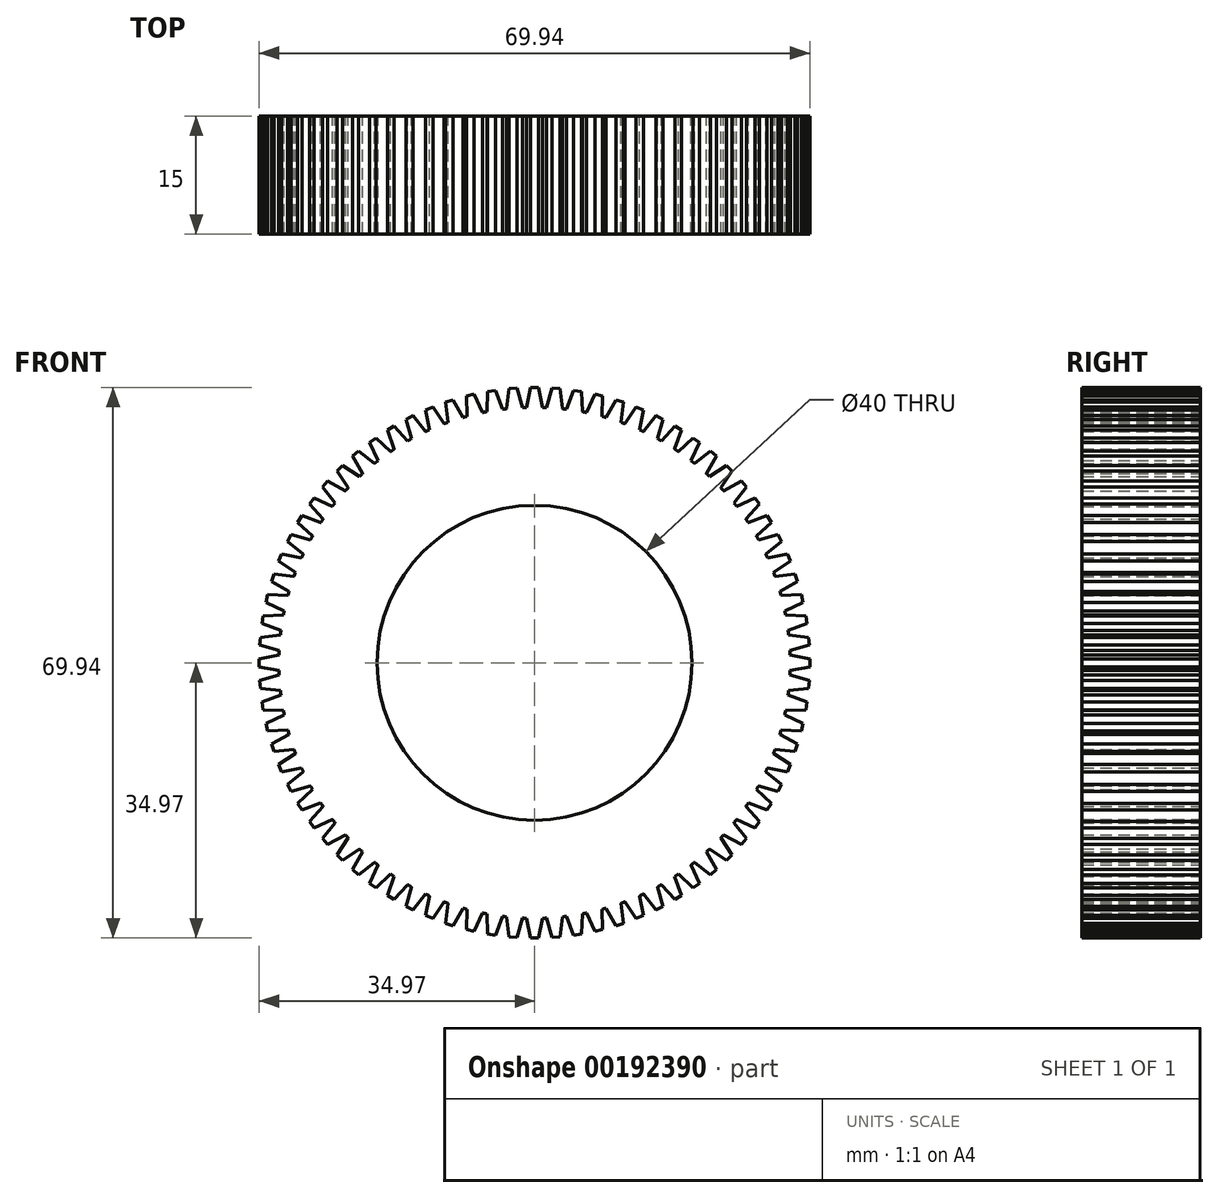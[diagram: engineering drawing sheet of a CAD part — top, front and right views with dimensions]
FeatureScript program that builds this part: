
annotation { "Feature Type Name" : "Feature", "Feature Type Description" : "" }
export const myFeature = defineFeature(function(context is Context, id is Id, definition is map)
    precondition{}
    {
        {
            var Q0;
            Q0=qCreatedBy(makeId("Front.planeOp"),FACE);
            var sketch = newSketch(context, id + "F0", { "sketchPlane" : qUnion([Q0])});
            skCircle(sketch, "E0", {"center": v(0, 0) * mm, "radius": 32.47 * mm});
            skLineSegment(sketch, "E1", {"start": v(-1, 32.45) * mm, "end": v(-0.5, 34.97) * mm});
            skLineSegment(sketch, "E2.MirrorCS", {"start": v(1, 32.45) * mm, "end": v(0.5, 34.97) * mm});
            skLineSegment(sketch, "E3", {"start": v(-0.5, 34.97) * mm, "end": v(0.5, 34.97) * mm});
            skLineSegment(sketch, "E4.1.0", {"start": v(-1.55, 32.43) * mm, "end": v(-2.25, 34.9) * mm});
            skLineSegment(sketch, "E4.1.1", {"start": v(-3.24, 34.82) * mm, "end": v(-2.25, 34.9) * mm});
            skLineSegment(sketch, "E4.1.2", {"start": v(-3.54, 32.27) * mm, "end": v(-3.24, 34.82) * mm});
            skLineSegment(sketch, "E4.2.0", {"start": v(-4.09, 32.21) * mm, "end": v(-4.98, 34.62) * mm});
            skLineSegment(sketch, "E4.2.1", {"start": v(-5.96, 34.46) * mm, "end": v(-4.98, 34.62) * mm});
            skLineSegment(sketch, "E4.2.2", {"start": v(-6.06, 31.9) * mm, "end": v(-5.96, 34.46) * mm});
            skLineSegment(sketch, "E4.3.0", {"start": v(-6.6, 31.8) * mm, "end": v(-7.68, 34.12) * mm});
            skLineSegment(sketch, "E4.3.1", {"start": v(-8.65, 33.89) * mm, "end": v(-7.68, 34.12) * mm});
            skLineSegment(sketch, "E4.3.2", {"start": v(-8.55, 31.32) * mm, "end": v(-8.65, 33.89) * mm});
            skLineSegment(sketch, "E4.4.0", {"start": v(-9.08, 31.17) * mm, "end": v(-10.33, 33.41) * mm});
            skLineSegment(sketch, "E4.4.1", {"start": v(-11.28, 33.1) * mm, "end": v(-10.33, 33.41) * mm});
            skLineSegment(sketch, "E4.4.2", {"start": v(-10.98, 30.56) * mm, "end": v(-11.28, 33.1) * mm});
            skLineSegment(sketch, "E4.5.0", {"start": v(-11.5, 30.37) * mm, "end": v(-12.92, 32.5) * mm});
            skLineSegment(sketch, "E4.5.1", {"start": v(-13.84, 32.12) * mm, "end": v(-12.92, 32.5) * mm});
            skLineSegment(sketch, "E4.5.2", {"start": v(-13.34, 29.6) * mm, "end": v(-13.84, 32.12) * mm});
            skLineSegment(sketch, "E4.6.0", {"start": v(-13.84, 29.37) * mm, "end": v(-15.43, 31.38) * mm});
            skLineSegment(sketch, "E4.6.1", {"start": v(-16.32, 30.93) * mm, "end": v(-15.43, 31.38) * mm});
            skLineSegment(sketch, "E4.6.2", {"start": v(-15.62, 28.46) * mm, "end": v(-16.32, 30.93) * mm});
            skLineSegment(sketch, "E4.7.0", {"start": v(-16.1, 28.2) * mm, "end": v(-17.84, 30.08) * mm});
            skLineSegment(sketch, "E4.7.1", {"start": v(-18.7, 29.55) * mm, "end": v(-17.84, 30.08) * mm});
            skLineSegment(sketch, "E4.7.2", {"start": v(-17.8, 27.15) * mm, "end": v(-18.7, 29.55) * mm});
            skLineSegment(sketch, "E4.8.0", {"start": v(-18.27, 26.84) * mm, "end": v(-20.15, 28.58) * mm});
            skLineSegment(sketch, "E4.8.1", {"start": v(-20.96, 28) * mm, "end": v(-20.15, 28.58) * mm});
            skLineSegment(sketch, "E4.8.2", {"start": v(-19.88, 25.67) * mm, "end": v(-20.96, 28) * mm});
            skLineSegment(sketch, "E4.9.0", {"start": v(-20.32, 25.33) * mm, "end": v(-22.33, 26.92) * mm});
            skLineSegment(sketch, "E4.9.1", {"start": v(-23.1, 26.27) * mm, "end": v(-22.33, 26.92) * mm});
            skLineSegment(sketch, "E4.9.2", {"start": v(-21.84, 24.03) * mm, "end": v(-23.1, 26.27) * mm});
            skLineSegment(sketch, "E4.10.0", {"start": v(-22.24, 23.65) * mm, "end": v(-24.37, 25.08) * mm});
            skLineSegment(sketch, "E4.10.1", {"start": v(-25.08, 24.37) * mm, "end": v(-24.37, 25.08) * mm});
            skLineSegment(sketch, "E4.10.2", {"start": v(-23.65, 22.24) * mm, "end": v(-25.08, 24.37) * mm});
            skLineSegment(sketch, "E4.11.0", {"start": v(-24.03, 21.84) * mm, "end": v(-26.27, 23.1) * mm});
            skLineSegment(sketch, "E4.11.1", {"start": v(-26.92, 22.33) * mm, "end": v(-26.27, 23.1) * mm});
            skLineSegment(sketch, "E4.11.2", {"start": v(-25.33, 20.32) * mm, "end": v(-26.92, 22.33) * mm});
            skLineSegment(sketch, "E4.12.0", {"start": v(-25.67, 19.88) * mm, "end": v(-28, 20.96) * mm});
            skLineSegment(sketch, "E4.12.1", {"start": v(-28.58, 20.15) * mm, "end": v(-28, 20.96) * mm});
            skLineSegment(sketch, "E4.12.2", {"start": v(-26.84, 18.27) * mm, "end": v(-28.58, 20.15) * mm});
            skLineSegment(sketch, "E4.13.0", {"start": v(-27.15, 17.8) * mm, "end": v(-29.55, 18.7) * mm});
            skLineSegment(sketch, "E4.13.1", {"start": v(-30.08, 17.84) * mm, "end": v(-29.55, 18.7) * mm});
            skLineSegment(sketch, "E4.13.2", {"start": v(-28.2, 16.1) * mm, "end": v(-30.08, 17.84) * mm});
            skLineSegment(sketch, "E4.14.0", {"start": v(-28.46, 15.62) * mm, "end": v(-30.93, 16.32) * mm});
            skLineSegment(sketch, "E4.14.1", {"start": v(-31.38, 15.43) * mm, "end": v(-30.93, 16.32) * mm});
            skLineSegment(sketch, "E4.14.2", {"start": v(-29.37, 13.84) * mm, "end": v(-31.38, 15.43) * mm});
            skLineSegment(sketch, "E4.15.0", {"start": v(-29.6, 13.34) * mm, "end": v(-32.12, 13.84) * mm});
            skLineSegment(sketch, "E4.15.1", {"start": v(-32.5, 12.92) * mm, "end": v(-32.12, 13.84) * mm});
            skLineSegment(sketch, "E4.15.2", {"start": v(-30.37, 11.5) * mm, "end": v(-32.5, 12.92) * mm});
            skLineSegment(sketch, "E4.16.0", {"start": v(-30.56, 10.98) * mm, "end": v(-33.1, 11.28) * mm});
            skLineSegment(sketch, "E4.16.1", {"start": v(-33.41, 10.33) * mm, "end": v(-33.1, 11.28) * mm});
            skLineSegment(sketch, "E4.16.2", {"start": v(-31.17, 9.08) * mm, "end": v(-33.41, 10.33) * mm});
            skLineSegment(sketch, "E4.17.0", {"start": v(-31.32, 8.55) * mm, "end": v(-33.89, 8.65) * mm});
            skLineSegment(sketch, "E4.17.1", {"start": v(-34.12, 7.68) * mm, "end": v(-33.89, 8.65) * mm});
            skLineSegment(sketch, "E4.17.2", {"start": v(-31.8, 6.6) * mm, "end": v(-34.12, 7.68) * mm});
            skLineSegment(sketch, "E4.18.0", {"start": v(-31.9, 6.06) * mm, "end": v(-34.46, 5.96) * mm});
            skLineSegment(sketch, "E4.18.1", {"start": v(-34.62, 4.98) * mm, "end": v(-34.46, 5.96) * mm});
            skLineSegment(sketch, "E4.18.2", {"start": v(-32.21, 4.09) * mm, "end": v(-34.62, 4.98) * mm});
            skLineSegment(sketch, "E4.19.0", {"start": v(-32.27, 3.54) * mm, "end": v(-34.82, 3.24) * mm});
            skLineSegment(sketch, "E4.19.1", {"start": v(-34.9, 2.25) * mm, "end": v(-34.82, 3.24) * mm});
            skLineSegment(sketch, "E4.19.2", {"start": v(-32.43, 1.55) * mm, "end": v(-34.9, 2.25) * mm});
            skLineSegment(sketch, "E4.20.0", {"start": v(-32.45, 1) * mm, "end": v(-34.97, 0.5) * mm});
            skLineSegment(sketch, "E4.20.1", {"start": v(-34.97, -0.5) * mm, "end": v(-34.97, 0.5) * mm});
            skLineSegment(sketch, "E4.20.2", {"start": v(-32.45, -1) * mm, "end": v(-34.97, -0.5) * mm});
            skLineSegment(sketch, "E4.21.0", {"start": v(-32.43, -1.55) * mm, "end": v(-34.9, -2.25) * mm});
            skLineSegment(sketch, "E4.21.1", {"start": v(-34.82, -3.24) * mm, "end": v(-34.9, -2.25) * mm});
            skLineSegment(sketch, "E4.21.2", {"start": v(-32.27, -3.54) * mm, "end": v(-34.82, -3.24) * mm});
            skLineSegment(sketch, "E4.22.0", {"start": v(-32.21, -4.09) * mm, "end": v(-34.62, -4.98) * mm});
            skLineSegment(sketch, "E4.22.1", {"start": v(-34.46, -5.96) * mm, "end": v(-34.62, -4.98) * mm});
            skLineSegment(sketch, "E4.22.2", {"start": v(-31.9, -6.06) * mm, "end": v(-34.46, -5.96) * mm});
            skLineSegment(sketch, "E4.23.0", {"start": v(-31.8, -6.6) * mm, "end": v(-34.12, -7.68) * mm});
            skLineSegment(sketch, "E4.23.1", {"start": v(-33.89, -8.65) * mm, "end": v(-34.12, -7.68) * mm});
            skLineSegment(sketch, "E4.23.2", {"start": v(-31.32, -8.55) * mm, "end": v(-33.89, -8.65) * mm});
            skLineSegment(sketch, "E4.24.0", {"start": v(-31.17, -9.08) * mm, "end": v(-33.41, -10.33) * mm});
            skLineSegment(sketch, "E4.24.1", {"start": v(-33.1, -11.28) * mm, "end": v(-33.41, -10.33) * mm});
            skLineSegment(sketch, "E4.24.2", {"start": v(-30.56, -10.98) * mm, "end": v(-33.1, -11.28) * mm});
            skLineSegment(sketch, "E4.25.0", {"start": v(-30.37, -11.5) * mm, "end": v(-32.5, -12.92) * mm});
            skLineSegment(sketch, "E4.25.1", {"start": v(-32.12, -13.84) * mm, "end": v(-32.5, -12.92) * mm});
            skLineSegment(sketch, "E4.25.2", {"start": v(-29.6, -13.34) * mm, "end": v(-32.12, -13.84) * mm});
            skLineSegment(sketch, "E4.26.0", {"start": v(-29.37, -13.84) * mm, "end": v(-31.38, -15.43) * mm});
            skLineSegment(sketch, "E4.26.1", {"start": v(-30.93, -16.32) * mm, "end": v(-31.38, -15.43) * mm});
            skLineSegment(sketch, "E4.26.2", {"start": v(-28.46, -15.62) * mm, "end": v(-30.93, -16.32) * mm});
            skLineSegment(sketch, "E4.27.0", {"start": v(-28.2, -16.1) * mm, "end": v(-30.08, -17.84) * mm});
            skLineSegment(sketch, "E4.27.1", {"start": v(-29.55, -18.7) * mm, "end": v(-30.08, -17.84) * mm});
            skLineSegment(sketch, "E4.27.2", {"start": v(-27.15, -17.8) * mm, "end": v(-29.55, -18.7) * mm});
            skLineSegment(sketch, "E4.28.0", {"start": v(-26.84, -18.27) * mm, "end": v(-28.58, -20.15) * mm});
            skLineSegment(sketch, "E4.28.1", {"start": v(-28, -20.96) * mm, "end": v(-28.58, -20.15) * mm});
            skLineSegment(sketch, "E4.28.2", {"start": v(-25.67, -19.88) * mm, "end": v(-28, -20.96) * mm});
            skLineSegment(sketch, "E4.29.0", {"start": v(-25.33, -20.32) * mm, "end": v(-26.92, -22.33) * mm});
            skLineSegment(sketch, "E4.29.1", {"start": v(-26.27, -23.1) * mm, "end": v(-26.92, -22.33) * mm});
            skLineSegment(sketch, "E4.29.2", {"start": v(-24.03, -21.84) * mm, "end": v(-26.27, -23.1) * mm});
            skLineSegment(sketch, "E4.30.0", {"start": v(-23.65, -22.24) * mm, "end": v(-25.08, -24.37) * mm});
            skLineSegment(sketch, "E4.30.1", {"start": v(-24.37, -25.08) * mm, "end": v(-25.08, -24.37) * mm});
            skLineSegment(sketch, "E4.30.2", {"start": v(-22.24, -23.65) * mm, "end": v(-24.37, -25.08) * mm});
            skLineSegment(sketch, "E4.31.0", {"start": v(-21.84, -24.03) * mm, "end": v(-23.1, -26.27) * mm});
            skLineSegment(sketch, "E4.31.1", {"start": v(-22.33, -26.92) * mm, "end": v(-23.1, -26.27) * mm});
            skLineSegment(sketch, "E4.31.2", {"start": v(-20.32, -25.33) * mm, "end": v(-22.33, -26.92) * mm});
            skLineSegment(sketch, "E4.32.0", {"start": v(-19.88, -25.67) * mm, "end": v(-20.96, -28) * mm});
            skLineSegment(sketch, "E4.32.1", {"start": v(-20.15, -28.58) * mm, "end": v(-20.96, -28) * mm});
            skLineSegment(sketch, "E4.32.2", {"start": v(-18.27, -26.84) * mm, "end": v(-20.15, -28.58) * mm});
            skLineSegment(sketch, "E4.33.0", {"start": v(-17.8, -27.15) * mm, "end": v(-18.7, -29.55) * mm});
            skLineSegment(sketch, "E4.33.1", {"start": v(-17.84, -30.08) * mm, "end": v(-18.7, -29.55) * mm});
            skLineSegment(sketch, "E4.33.2", {"start": v(-16.1, -28.2) * mm, "end": v(-17.84, -30.08) * mm});
            skLineSegment(sketch, "E4.34.0", {"start": v(-15.62, -28.46) * mm, "end": v(-16.32, -30.93) * mm});
            skLineSegment(sketch, "E4.34.1", {"start": v(-15.43, -31.38) * mm, "end": v(-16.32, -30.93) * mm});
            skLineSegment(sketch, "E4.34.2", {"start": v(-13.84, -29.37) * mm, "end": v(-15.43, -31.38) * mm});
            skLineSegment(sketch, "E4.35.0", {"start": v(-13.34, -29.6) * mm, "end": v(-13.84, -32.12) * mm});
            skLineSegment(sketch, "E4.35.1", {"start": v(-12.92, -32.5) * mm, "end": v(-13.84, -32.12) * mm});
            skLineSegment(sketch, "E4.35.2", {"start": v(-11.5, -30.37) * mm, "end": v(-12.92, -32.5) * mm});
            skLineSegment(sketch, "E4.36.0", {"start": v(-10.98, -30.56) * mm, "end": v(-11.28, -33.1) * mm});
            skLineSegment(sketch, "E4.36.1", {"start": v(-10.33, -33.41) * mm, "end": v(-11.28, -33.1) * mm});
            skLineSegment(sketch, "E4.36.2", {"start": v(-9.08, -31.17) * mm, "end": v(-10.33, -33.41) * mm});
            skLineSegment(sketch, "E4.37.0", {"start": v(-8.55, -31.32) * mm, "end": v(-8.65, -33.89) * mm});
            skLineSegment(sketch, "E4.37.1", {"start": v(-7.68, -34.12) * mm, "end": v(-8.65, -33.89) * mm});
            skLineSegment(sketch, "E4.37.2", {"start": v(-6.6, -31.8) * mm, "end": v(-7.68, -34.12) * mm});
            skLineSegment(sketch, "E4.38.0", {"start": v(-6.06, -31.9) * mm, "end": v(-5.96, -34.46) * mm});
            skLineSegment(sketch, "E4.38.1", {"start": v(-4.98, -34.62) * mm, "end": v(-5.96, -34.46) * mm});
            skLineSegment(sketch, "E4.38.2", {"start": v(-4.09, -32.21) * mm, "end": v(-4.98, -34.62) * mm});
            skLineSegment(sketch, "E4.39.0", {"start": v(-3.54, -32.27) * mm, "end": v(-3.24, -34.82) * mm});
            skLineSegment(sketch, "E4.39.1", {"start": v(-2.25, -34.9) * mm, "end": v(-3.24, -34.82) * mm});
            skLineSegment(sketch, "E4.39.2", {"start": v(-1.55, -32.43) * mm, "end": v(-2.25, -34.9) * mm});
            skLineSegment(sketch, "E4.40.0", {"start": v(-1, -32.45) * mm, "end": v(-0.5, -34.97) * mm});
            skLineSegment(sketch, "E4.40.1", {"start": v(0.5, -34.97) * mm, "end": v(-0.5, -34.97) * mm});
            skLineSegment(sketch, "E4.40.2", {"start": v(1, -32.45) * mm, "end": v(0.5, -34.97) * mm});
            skLineSegment(sketch, "E4.41.0", {"start": v(1.55, -32.43) * mm, "end": v(2.25, -34.9) * mm});
            skLineSegment(sketch, "E4.41.1", {"start": v(3.24, -34.82) * mm, "end": v(2.25, -34.9) * mm});
            skLineSegment(sketch, "E4.41.2", {"start": v(3.54, -32.27) * mm, "end": v(3.24, -34.82) * mm});
            skLineSegment(sketch, "E4.42.0", {"start": v(4.09, -32.21) * mm, "end": v(4.98, -34.62) * mm});
            skLineSegment(sketch, "E4.42.1", {"start": v(5.96, -34.46) * mm, "end": v(4.98, -34.62) * mm});
            skLineSegment(sketch, "E4.42.2", {"start": v(6.06, -31.9) * mm, "end": v(5.96, -34.46) * mm});
            skLineSegment(sketch, "E4.43.0", {"start": v(6.6, -31.8) * mm, "end": v(7.68, -34.12) * mm});
            skLineSegment(sketch, "E4.43.1", {"start": v(8.65, -33.89) * mm, "end": v(7.68, -34.12) * mm});
            skLineSegment(sketch, "E4.43.2", {"start": v(8.55, -31.32) * mm, "end": v(8.65, -33.89) * mm});
            skLineSegment(sketch, "E4.44.0", {"start": v(9.08, -31.17) * mm, "end": v(10.33, -33.41) * mm});
            skLineSegment(sketch, "E4.44.1", {"start": v(11.28, -33.1) * mm, "end": v(10.33, -33.41) * mm});
            skLineSegment(sketch, "E4.44.2", {"start": v(10.98, -30.56) * mm, "end": v(11.28, -33.1) * mm});
            skLineSegment(sketch, "E4.45.0", {"start": v(11.5, -30.37) * mm, "end": v(12.92, -32.5) * mm});
            skLineSegment(sketch, "E4.45.1", {"start": v(13.84, -32.12) * mm, "end": v(12.92, -32.5) * mm});
            skLineSegment(sketch, "E4.45.2", {"start": v(13.34, -29.6) * mm, "end": v(13.84, -32.12) * mm});
            skLineSegment(sketch, "E4.46.0", {"start": v(13.84, -29.37) * mm, "end": v(15.43, -31.38) * mm});
            skLineSegment(sketch, "E4.46.1", {"start": v(16.32, -30.93) * mm, "end": v(15.43, -31.38) * mm});
            skLineSegment(sketch, "E4.46.2", {"start": v(15.62, -28.46) * mm, "end": v(16.32, -30.93) * mm});
            skLineSegment(sketch, "E4.47.0", {"start": v(16.1, -28.2) * mm, "end": v(17.84, -30.08) * mm});
            skLineSegment(sketch, "E4.47.1", {"start": v(18.7, -29.55) * mm, "end": v(17.84, -30.08) * mm});
            skLineSegment(sketch, "E4.47.2", {"start": v(17.8, -27.15) * mm, "end": v(18.7, -29.55) * mm});
            skLineSegment(sketch, "E4.48.0", {"start": v(18.27, -26.84) * mm, "end": v(20.15, -28.58) * mm});
            skLineSegment(sketch, "E4.48.1", {"start": v(20.96, -28) * mm, "end": v(20.15, -28.58) * mm});
            skLineSegment(sketch, "E4.48.2", {"start": v(19.88, -25.67) * mm, "end": v(20.96, -28) * mm});
            skLineSegment(sketch, "E4.49.0", {"start": v(20.32, -25.33) * mm, "end": v(22.33, -26.92) * mm});
            skLineSegment(sketch, "E4.49.1", {"start": v(23.1, -26.27) * mm, "end": v(22.33, -26.92) * mm});
            skLineSegment(sketch, "E4.49.2", {"start": v(21.84, -24.03) * mm, "end": v(23.1, -26.27) * mm});
            skLineSegment(sketch, "E4.50.0", {"start": v(22.24, -23.65) * mm, "end": v(24.37, -25.08) * mm});
            skLineSegment(sketch, "E4.50.1", {"start": v(25.08, -24.37) * mm, "end": v(24.37, -25.08) * mm});
            skLineSegment(sketch, "E4.50.2", {"start": v(23.65, -22.24) * mm, "end": v(25.08, -24.37) * mm});
            skLineSegment(sketch, "E4.51.0", {"start": v(24.03, -21.84) * mm, "end": v(26.27, -23.1) * mm});
            skLineSegment(sketch, "E4.51.1", {"start": v(26.92, -22.33) * mm, "end": v(26.27, -23.1) * mm});
            skLineSegment(sketch, "E4.51.2", {"start": v(25.33, -20.32) * mm, "end": v(26.92, -22.33) * mm});
            skLineSegment(sketch, "E4.52.0", {"start": v(25.67, -19.88) * mm, "end": v(28, -20.96) * mm});
            skLineSegment(sketch, "E4.52.1", {"start": v(28.58, -20.15) * mm, "end": v(28, -20.96) * mm});
            skLineSegment(sketch, "E4.52.2", {"start": v(26.84, -18.27) * mm, "end": v(28.58, -20.15) * mm});
            skLineSegment(sketch, "E4.53.0", {"start": v(27.15, -17.8) * mm, "end": v(29.55, -18.7) * mm});
            skLineSegment(sketch, "E4.53.1", {"start": v(30.08, -17.84) * mm, "end": v(29.55, -18.7) * mm});
            skLineSegment(sketch, "E4.53.2", {"start": v(28.2, -16.1) * mm, "end": v(30.08, -17.84) * mm});
            skLineSegment(sketch, "E4.54.0", {"start": v(28.46, -15.62) * mm, "end": v(30.93, -16.32) * mm});
            skLineSegment(sketch, "E4.54.1", {"start": v(31.38, -15.43) * mm, "end": v(30.93, -16.32) * mm});
            skLineSegment(sketch, "E4.54.2", {"start": v(29.37, -13.84) * mm, "end": v(31.38, -15.43) * mm});
            skLineSegment(sketch, "E4.55.0", {"start": v(29.6, -13.34) * mm, "end": v(32.12, -13.84) * mm});
            skLineSegment(sketch, "E4.55.1", {"start": v(32.5, -12.92) * mm, "end": v(32.12, -13.84) * mm});
            skLineSegment(sketch, "E4.55.2", {"start": v(30.37, -11.5) * mm, "end": v(32.5, -12.92) * mm});
            skLineSegment(sketch, "E4.56.0", {"start": v(30.56, -10.98) * mm, "end": v(33.1, -11.28) * mm});
            skLineSegment(sketch, "E4.56.1", {"start": v(33.41, -10.33) * mm, "end": v(33.1, -11.28) * mm});
            skLineSegment(sketch, "E4.56.2", {"start": v(31.17, -9.08) * mm, "end": v(33.41, -10.33) * mm});
            skLineSegment(sketch, "E4.57.0", {"start": v(31.32, -8.55) * mm, "end": v(33.89, -8.65) * mm});
            skLineSegment(sketch, "E4.57.1", {"start": v(34.12, -7.68) * mm, "end": v(33.89, -8.65) * mm});
            skLineSegment(sketch, "E4.57.2", {"start": v(31.8, -6.6) * mm, "end": v(34.12, -7.68) * mm});
            skLineSegment(sketch, "E4.58.0", {"start": v(31.9, -6.06) * mm, "end": v(34.46, -5.96) * mm});
            skLineSegment(sketch, "E4.58.1", {"start": v(34.62, -4.98) * mm, "end": v(34.46, -5.96) * mm});
            skLineSegment(sketch, "E4.58.2", {"start": v(32.21, -4.09) * mm, "end": v(34.62, -4.98) * mm});
            skLineSegment(sketch, "E4.59.0", {"start": v(32.27, -3.54) * mm, "end": v(34.82, -3.24) * mm});
            skLineSegment(sketch, "E4.59.1", {"start": v(34.9, -2.25) * mm, "end": v(34.82, -3.24) * mm});
            skLineSegment(sketch, "E4.59.2", {"start": v(32.43, -1.55) * mm, "end": v(34.9, -2.25) * mm});
            skLineSegment(sketch, "E4.60.0", {"start": v(32.45, -1) * mm, "end": v(34.97, -0.5) * mm});
            skLineSegment(sketch, "E4.60.1", {"start": v(34.97, 0.5) * mm, "end": v(34.97, -0.5) * mm});
            skLineSegment(sketch, "E4.60.2", {"start": v(32.45, 1) * mm, "end": v(34.97, 0.5) * mm});
            skLineSegment(sketch, "E4.61.0", {"start": v(32.43, 1.55) * mm, "end": v(34.9, 2.25) * mm});
            skLineSegment(sketch, "E4.61.1", {"start": v(34.82, 3.24) * mm, "end": v(34.9, 2.25) * mm});
            skLineSegment(sketch, "E4.61.2", {"start": v(32.27, 3.54) * mm, "end": v(34.82, 3.24) * mm});
            skLineSegment(sketch, "E4.62.0", {"start": v(32.21, 4.09) * mm, "end": v(34.62, 4.98) * mm});
            skLineSegment(sketch, "E4.62.1", {"start": v(34.46, 5.96) * mm, "end": v(34.62, 4.98) * mm});
            skLineSegment(sketch, "E4.62.2", {"start": v(31.9, 6.06) * mm, "end": v(34.46, 5.96) * mm});
            skLineSegment(sketch, "E4.63.0", {"start": v(31.8, 6.6) * mm, "end": v(34.12, 7.68) * mm});
            skLineSegment(sketch, "E4.63.1", {"start": v(33.89, 8.65) * mm, "end": v(34.12, 7.68) * mm});
            skLineSegment(sketch, "E4.63.2", {"start": v(31.32, 8.55) * mm, "end": v(33.89, 8.65) * mm});
            skLineSegment(sketch, "E4.64.0", {"start": v(31.17, 9.08) * mm, "end": v(33.41, 10.33) * mm});
            skLineSegment(sketch, "E4.64.1", {"start": v(33.1, 11.28) * mm, "end": v(33.41, 10.33) * mm});
            skLineSegment(sketch, "E4.64.2", {"start": v(30.56, 10.98) * mm, "end": v(33.1, 11.28) * mm});
            skLineSegment(sketch, "E4.65.0", {"start": v(30.37, 11.5) * mm, "end": v(32.5, 12.92) * mm});
            skLineSegment(sketch, "E4.65.1", {"start": v(32.12, 13.84) * mm, "end": v(32.5, 12.92) * mm});
            skLineSegment(sketch, "E4.65.2", {"start": v(29.6, 13.34) * mm, "end": v(32.12, 13.84) * mm});
            skLineSegment(sketch, "E4.66.0", {"start": v(29.37, 13.84) * mm, "end": v(31.38, 15.43) * mm});
            skLineSegment(sketch, "E4.66.1", {"start": v(30.93, 16.32) * mm, "end": v(31.38, 15.43) * mm});
            skLineSegment(sketch, "E4.66.2", {"start": v(28.46, 15.62) * mm, "end": v(30.93, 16.32) * mm});
            skLineSegment(sketch, "E4.67.0", {"start": v(28.2, 16.1) * mm, "end": v(30.08, 17.84) * mm});
            skLineSegment(sketch, "E4.67.1", {"start": v(29.55, 18.7) * mm, "end": v(30.08, 17.84) * mm});
            skLineSegment(sketch, "E4.67.2", {"start": v(27.15, 17.8) * mm, "end": v(29.55, 18.7) * mm});
            skLineSegment(sketch, "E4.68.0", {"start": v(26.84, 18.27) * mm, "end": v(28.58, 20.15) * mm});
            skLineSegment(sketch, "E4.68.1", {"start": v(28, 20.96) * mm, "end": v(28.58, 20.15) * mm});
            skLineSegment(sketch, "E4.68.2", {"start": v(25.67, 19.88) * mm, "end": v(28, 20.96) * mm});
            skLineSegment(sketch, "E4.69.0", {"start": v(25.33, 20.32) * mm, "end": v(26.92, 22.33) * mm});
            skLineSegment(sketch, "E4.69.1", {"start": v(26.27, 23.1) * mm, "end": v(26.92, 22.33) * mm});
            skLineSegment(sketch, "E4.69.2", {"start": v(24.03, 21.84) * mm, "end": v(26.27, 23.1) * mm});
            skLineSegment(sketch, "E4.70.0", {"start": v(23.65, 22.24) * mm, "end": v(25.08, 24.37) * mm});
            skLineSegment(sketch, "E4.70.1", {"start": v(24.37, 25.08) * mm, "end": v(25.08, 24.37) * mm});
            skLineSegment(sketch, "E4.70.2", {"start": v(22.24, 23.65) * mm, "end": v(24.37, 25.08) * mm});
            skLineSegment(sketch, "E4.71.0", {"start": v(21.84, 24.03) * mm, "end": v(23.1, 26.27) * mm});
            skLineSegment(sketch, "E4.71.1", {"start": v(22.33, 26.92) * mm, "end": v(23.1, 26.27) * mm});
            skLineSegment(sketch, "E4.71.2", {"start": v(20.32, 25.33) * mm, "end": v(22.33, 26.92) * mm});
            skLineSegment(sketch, "E4.72.0", {"start": v(19.88, 25.67) * mm, "end": v(20.96, 28) * mm});
            skLineSegment(sketch, "E4.72.1", {"start": v(20.15, 28.58) * mm, "end": v(20.96, 28) * mm});
            skLineSegment(sketch, "E4.72.2", {"start": v(18.27, 26.84) * mm, "end": v(20.15, 28.58) * mm});
            skLineSegment(sketch, "E4.73.0", {"start": v(17.8, 27.15) * mm, "end": v(18.7, 29.55) * mm});
            skLineSegment(sketch, "E4.73.1", {"start": v(17.84, 30.08) * mm, "end": v(18.7, 29.55) * mm});
            skLineSegment(sketch, "E4.73.2", {"start": v(16.1, 28.2) * mm, "end": v(17.84, 30.08) * mm});
            skLineSegment(sketch, "E4.74.0", {"start": v(15.62, 28.46) * mm, "end": v(16.32, 30.93) * mm});
            skLineSegment(sketch, "E4.74.1", {"start": v(15.43, 31.38) * mm, "end": v(16.32, 30.93) * mm});
            skLineSegment(sketch, "E4.74.2", {"start": v(13.84, 29.37) * mm, "end": v(15.43, 31.38) * mm});
            skLineSegment(sketch, "E4.75.0", {"start": v(13.34, 29.6) * mm, "end": v(13.84, 32.12) * mm});
            skLineSegment(sketch, "E4.75.1", {"start": v(12.92, 32.5) * mm, "end": v(13.84, 32.12) * mm});
            skLineSegment(sketch, "E4.75.2", {"start": v(11.5, 30.37) * mm, "end": v(12.92, 32.5) * mm});
            skLineSegment(sketch, "E4.76.0", {"start": v(10.98, 30.56) * mm, "end": v(11.28, 33.1) * mm});
            skLineSegment(sketch, "E4.76.1", {"start": v(10.33, 33.41) * mm, "end": v(11.28, 33.1) * mm});
            skLineSegment(sketch, "E4.76.2", {"start": v(9.08, 31.17) * mm, "end": v(10.33, 33.41) * mm});
            skLineSegment(sketch, "E4.77.0", {"start": v(8.55, 31.32) * mm, "end": v(8.65, 33.89) * mm});
            skLineSegment(sketch, "E4.77.1", {"start": v(7.68, 34.12) * mm, "end": v(8.65, 33.89) * mm});
            skLineSegment(sketch, "E4.77.2", {"start": v(6.6, 31.8) * mm, "end": v(7.68, 34.12) * mm});
            skLineSegment(sketch, "E4.78.0", {"start": v(6.06, 31.9) * mm, "end": v(5.96, 34.46) * mm});
            skLineSegment(sketch, "E4.78.1", {"start": v(4.98, 34.62) * mm, "end": v(5.96, 34.46) * mm});
            skLineSegment(sketch, "E4.78.2", {"start": v(4.09, 32.21) * mm, "end": v(4.98, 34.62) * mm});
            skLineSegment(sketch, "E4.79.0", {"start": v(3.54, 32.27) * mm, "end": v(3.24, 34.82) * mm});
            skLineSegment(sketch, "E4.79.1", {"start": v(2.25, 34.9) * mm, "end": v(3.24, 34.82) * mm});
            skLineSegment(sketch, "E4.79.2", {"start": v(1.55, 32.43) * mm, "end": v(2.25, 34.9) * mm});
            skSolve(sketch);
        }
        {
            var Q0;
            Q0 = qSketchRegion(id + "F0", true);
            extrude(context, id + "F1", {"entities" : qUnion([Q0]), "depth" : 15 * mm});
        }
        {
            var Q0;
            Q0=qCreatedBy(makeId("Front.planeOp"),FACE);
            var sketch = newSketch(context, id + "F2", { "sketchPlane" : qUnion([Q0])});
            skCircle(sketch, "E5", {"center": v(0, 0) * mm, "radius": 20 * mm});
            skSolve(sketch);
        }
        {
            var Q0;
            Q0 = qSketchRegion(id + "F2", true);
            extrude(context, id + "F3", {"entities" : qUnion([Q0]), "operationType" : NewBodyOperationType.REMOVE, "endBound" : BoundingType.THROUGH_ALL, "depth" : 25 * mm});
        }
    });
